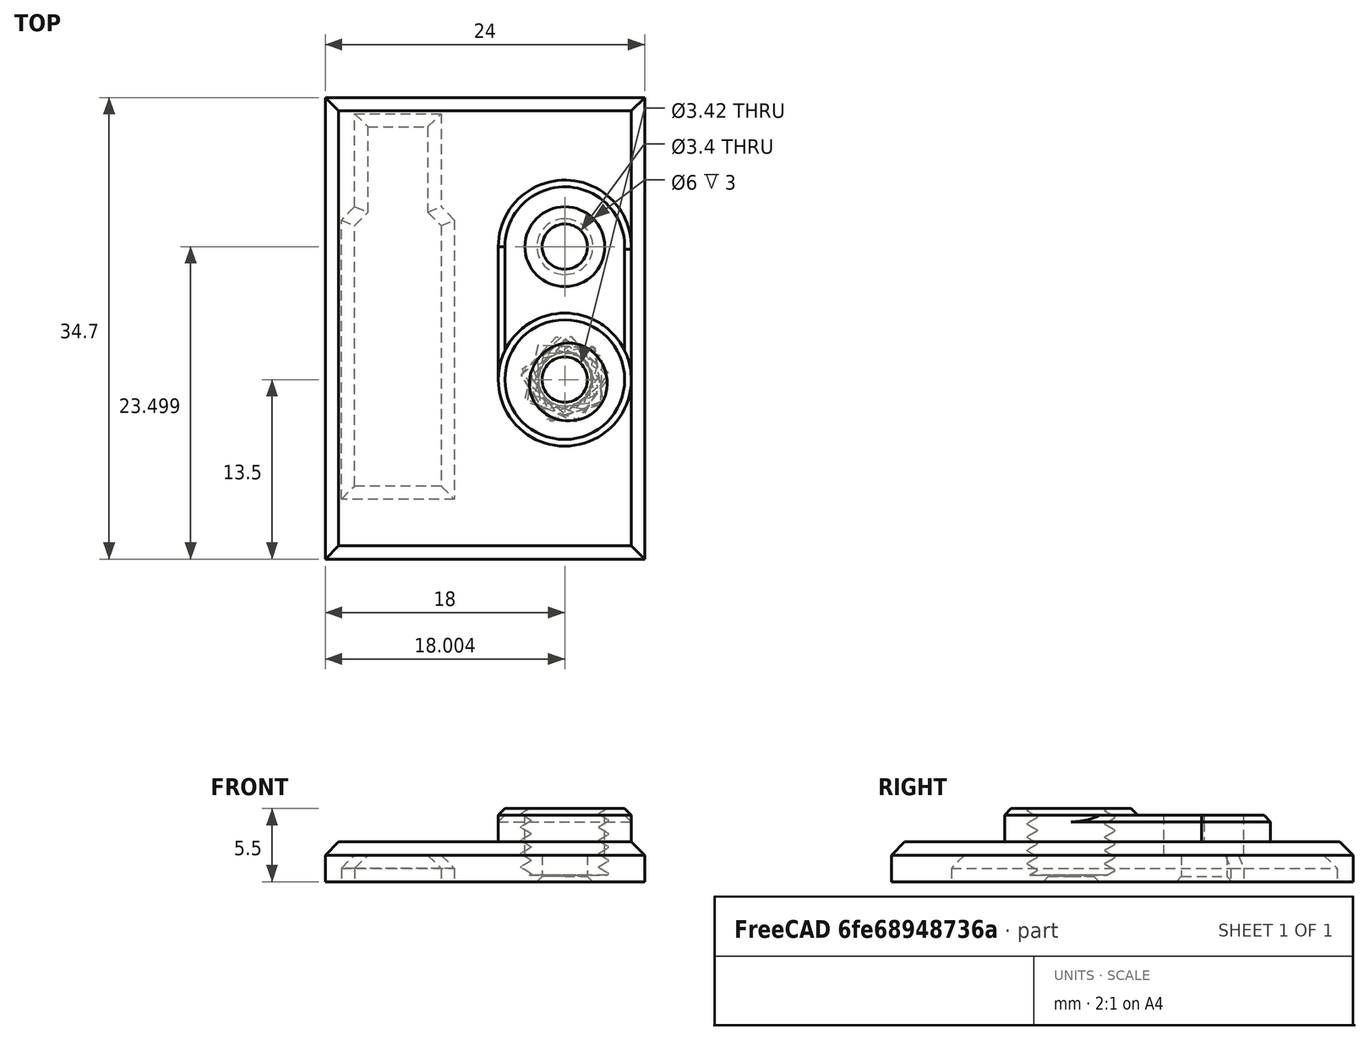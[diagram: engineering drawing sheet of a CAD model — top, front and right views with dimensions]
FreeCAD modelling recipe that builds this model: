
FCSTD DOCUMENT  (FreeCAD 0.18R14555 (Git shallow))
Label: filament-coder
License: All rights reserved
LicenseURL: http://en.wikipedia.org/wiki/All_rights_reserved
objects: Part::Cylinder×5, Part::Cut×5, Part::Chamfer×3, Part::Feature×2, Part::MultiFuse×2, Part::Box×1
note: 18 computed .brp shape members not serialized (recipe doc carries the construction recipe); baked Part::Feature solids carry a one-line shape summary decoded from their .brp

FEATURE [Part::Feature] Part__Feature007  label="Sensor Cover MK3s"
  Placement = pos=(6.0038,11.1986,-2.08622e-09) rot=(0,-0.707107,-0.707107;3.14159rad)
  shape: bbox 24.01 x 34.71 x 5.028 mm, 43 faces (baked)
FEATURE [Part::Cylinder] Cylinder
  Angle = 360
  AttacherType = Attacher::AttachEngine3D
  Height = 5.5
  Radius = 5
FEATURE [Part::Chamfer] Chamfer
  Base = -> Cylinder
  Edges = 1 edges r=0.5: [Edge1]
  Placement = pos=(0,-10,0) rot=(0,0,1;0rad)
FEATURE [Part::Cylinder] Cylinder001
  Angle = 360
  AttacherType = Attacher::AttachEngine3D
  Height = 10
  Placement = pos=(0,-10,0) rot=(0,0,1;0rad)
  Radius = 1.71
FEATURE [Part::MultiFuse] Fusion
  Shapes = -> [Part__Feature007,Chamfer]
FEATURE [Part::Cut] Cut
  Base = -> Fusion
  Tool = -> Cylinder001
FEATURE [Part::Chamfer] Chamfer001
  Base = -> Cut
  Edges = 3 edges r=0.4: [Edge2,Edge15,Edge16]
FEATURE [Part::Feature] Part__Feature  label="1"
  shape: bbox 11.55 x 19.8 x 11.8 mm, 29 faces (baked)
FEATURE [Part::Cylinder] Cylinder002
  Angle = 360
  AttacherType = Attacher::AttachEngine3D
  Height = 6
  Radius = 4
FEATURE [Part::Cut] Cut001
  Base = -> Cylinder002
  Placement = pos=(0,-10,0.5) rot=(0,0,1;0rad)
  Tool = -> Part__Feature
FEATURE [Part::Cut] Cut002
  Base = -> Chamfer001
  Tool = -> Cut001
FEATURE [Part::Box] Box  label="Cube"
  AttacherType = Attacher::AttachEngine3D
  Height = 2.5
  Length = 10
  Placement = pos=(-5,-10,2.5) rot=(0,0,1;0rad)
  Width = 10
FEATURE [Part::Chamfer] Chamfer002
  Base = -> Box
  Edges = 2 edges r=0.5: [Edge2,Edge6]
FEATURE [Part::Cylinder] Cylinder003
  Angle = 360
  AttacherType = Attacher::AttachEngine3D
  Height = 10
  Radius = 4
FEATURE [Part::Cut] Cut003
  Base = -> Chamfer002
  Tool = -> Cylinder003
FEATURE [Part::Cylinder] Cylinder004
  Angle = 360
  AttacherType = Attacher::AttachEngine3D
  Height = 10
  Placement = pos=(0,-10,0) rot=(0,0,1;0rad)
  Radius = 4.5
FEATURE [Part::Cut] Cut004
  Base = -> Cut003
  Tool = -> Cylinder004
FEATURE [Part::MultiFuse] Fusion001
  Shapes = -> [Cut002,Cut004]
